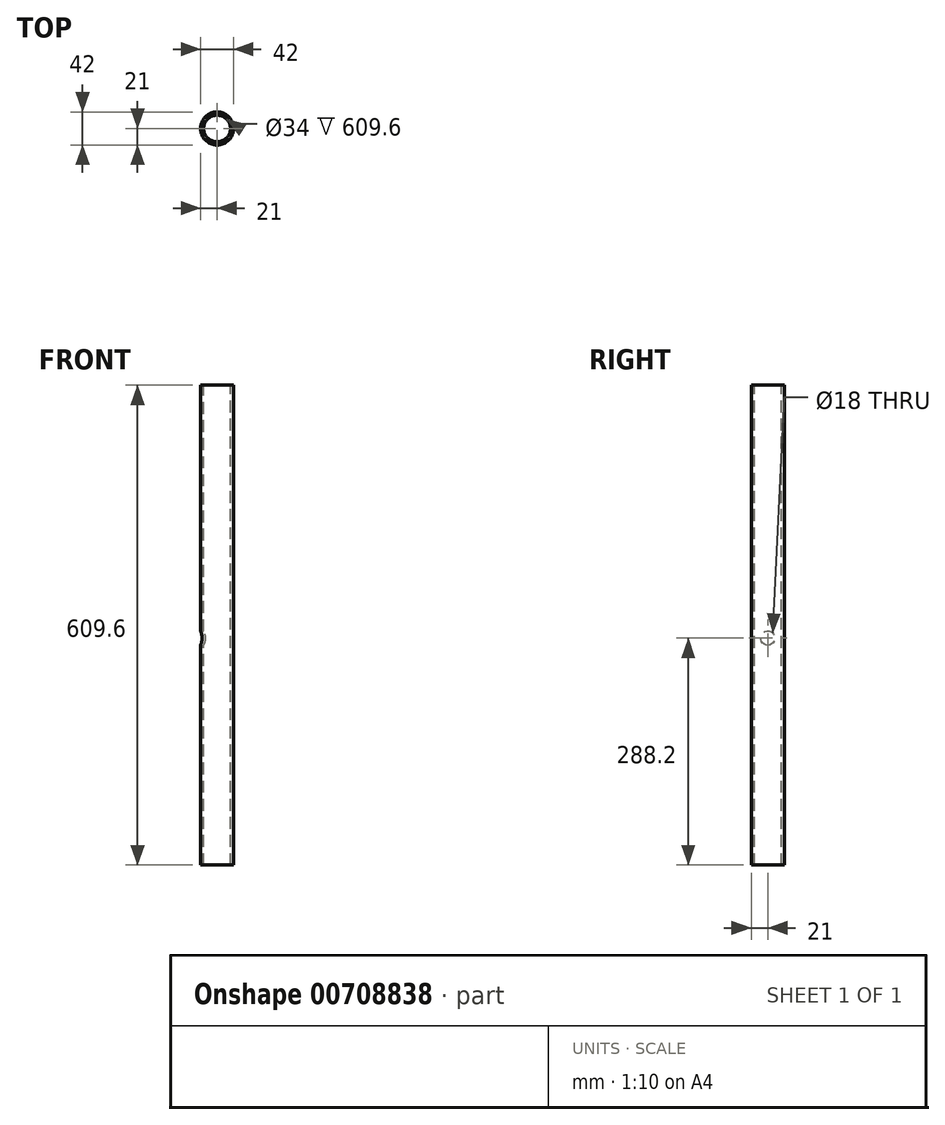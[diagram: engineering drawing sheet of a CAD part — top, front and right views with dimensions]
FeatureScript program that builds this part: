
annotation { "Feature Type Name" : "Feature", "Feature Type Description" : "" }
export const myFeature = defineFeature(function(context is Context, id is Id, definition is map)
    precondition{}
    {
        {
            var Q0;
            Q0=qCreatedBy(makeId("Front.planeOp"),FACE);
            var sketch = newSketch(context, id + "F0", { "sketchPlane" : qUnion([Q0])});
            skLineSegment(sketch, "E0", {"start": v(0, 270.85) * mm, "end": v(0, -338.75) * mm});
            skLineSegment(sketch, "E1", {"start": v(21, 271.4) * mm, "end": v(21, -338.2) * mm});
            skLineSegment(sketch, "E2", {"start": v(21, -338.2) * mm, "end": v(17, -338.2) * mm});
            skLineSegment(sketch, "E3", {"start": v(17, -338.2) * mm, "end": v(17, 271.4) * mm});
            skLineSegment(sketch, "E4", {"start": v(21, 271.4) * mm, "end": v(17, 271.4) * mm});
            skSolve(sketch);
        }
        {
            var Q0;
            Q0=qSketchRegion(id+"F0",true);
            var Q1;
            Q1=sQuery(id+"F0.wireOp",EDGE,"E0");
            revolve(context, id + "F1", {"surfaceOperationType" : NewSurfaceOperationType.NEW, "entities" : qUnion([Q0]), "axis" : qUnion([Q1]), "revolveType" : RevolveType.FULL});
        }
        {
            var Q0;
            Q0=qCreatedBy(makeId("Right.planeOp"),FACE);
            var sketch = newSketch(context, id + "F2", { "sketchPlane" : qUnion([Q0])});
            skCircle(sketch, "E5", {"center": v(0, -50) * mm, "radius": 9 * mm});
            skSolve(sketch);
        }
        {
            var Q0;
            Q0=qSketchRegion(id+"F2",true);
            extrude(context, id + "F3", {"entities" : qUnion([Q0]), "operationType" : NewBodyOperationType.REMOVE, "endBound" : BoundingType.THROUGH_ALL, "oppositeDirection" : true, "depth" : 25 * mm, "offsetDistance" : 25 * mm});
        }
    });
